# Revit family: BORGE_Вертикальная пожарная лестница_П-1
name_source: partatom
category: Обобщенные модели
units: mm (PartAtom-declared; Revit-internal decimal feet)

## family parameters
Всегда вертикально = Да
Заголовок OmniClass = Diffusers, Registers, and Grilles
Может служить основой для арматурных стержней = Нет
На основе рабочей плоскости = Нет
Номер OmniClass = 23.75.70.21.27.11
Общий = Нет
При загрузке вырезать с полостями = Нет
Размер круглого соединителя = Использовать диаметр
Тип детали = Нормальный
Точка расчета площади = Нет

## types (22) — shared parameters
ADSK_URL документации изделия = https://borge.pro
ADSK_URL страницы изделия = https://borge.pro
ADSK_Версия семейства = Rev1 2023-08
BIM Support_Разрабочик = BIM Support
BIM Support_Сайт = https://www.bim-support.ru
LT = BORGE_Снегозадержатель_Трубчатый
URL = https://borge.ru
Изготовитель = ООО «Борге», ООО «Бипро»
Описание = Максимальная высота лестницы 6м.

## per-type parameters (varying)
| type | ADSK_Материал | Code2 |
| Пожарная лестница_П1-1_Бело-алюминиевый_RAL 9006 | BOGRE_Уcловный_Коричневый шоколад_RAL 8017 | 10 |
| Пожарная лестница_П1-1_Чёрный матовый_RAL 9005 | BOGRE_Уcловный_Чёрный матовый_RAL 9005 | 2 |
| Пожарная лестница_П1-1_Чёрный_RAL 9005 | BOGRE_Уcловный_Чёрный_RAL 9005 | 3 |
| Пожарная лестница_П1-1_Сигнально-белый_RAL 9003 | BOGRE_Уcловный_Сигнально-белый_RAL 9003 | 4 |
| Пожарная лестница_П1-1_Окрашенный_NL 807 | BOGRE_Уcловный_Окрашенный_NL 807 | 5 |
| Пожарная лестница_П1-1_Окрашенный_NL 805 | BOGRE_Уcловный_Окрашенный_NL 805 | 6 |
| Пожарная лестница_П1-1_Серо-коричневый матовый_RAL 8019 | BOGRE_Уcловный_Серо-коричневый матовый_RAL 8019 | 7 |
| Пожарная лестница_П1-1_Серо-коричневый_RAL 8019 | BOGRE_Уcловный_Серо-коричневый_RAL 8019 | 8 |
| Пожарная лестница_П1-1_Коричневый шоколад матовый_RAL 8017 | BOGRE_Уcловный_Коричневый шоколад матовый_RAL 8017 | 9 |
| Пожарная лестница_П1-1_Коричневый шоколад_RAL 8017 | BOGRE_Уcловный_Коричневый шоколад_RAL 8017 | 10 |
| Пожарная лестница_П1-1_Терракотовый_RAL 8004 | BOGRE_Уcловный_Терракотовый_RAL 8004 | 11 |
| Пожарная лестница_П1-1_Серый графит матовый_RAL 7024 | BOGRE_Уcловный_Серый графит матовый_RAL 7024 | 12 |
| Пожарная лестница_П1-1_Серый графит_RAL 7024 | BOGRE_Уcловный_Серый графит_RAL 7024 | 13 |
| Пожарная лестница_П1-1_Антрацитово-серый_RAL 7016 | BOGRE_Уcловный_Антрацитово-серый_RAL 7016 | 14 |
| Пожарная лестница_П1-1_Сигнально-серый_RAL 7004 | BOGRE_Уcловный_Сигнально-серый_RAL 7004 | 15 |
| Пожарная лестница_П1-1_Зелёный мох_RAL 6005 | BOGRE_Уcловный_Зелёный мох_RAL 6005 | 16 |
| Пожарная лестница_П1-1_Лиственно-зеленый_RAL 6002 | BOGRE_Уcловный_Лиственно-зеленый_RAL 6002 | 17 |
| Пожарная лестница_П1-1_Сигнально-синий_RAL 5005 | BOGRE_Уcловный_Сигнально-синий_RAL 5005 | 18 |
| Пожарная лестница_П1-1_Серо-коричневый_RR 32 | BOGRE_Уcловный_Серо-коричневый_RR 32 | 19 |
| Пожарная лестница_П1-1_Коричнево-красный_RAL 3011 | BOGRE_Уcловный_Коричнево-красный_RAL 3011 | 20 |
| Пожарная лестница_П1-1_Красное вино_RAL 3005 | BOGRE_Уcловный_Красное вино_RAL 3005 | 21 |
| Пожарная лестница_П1-1_Рубиново-красный_RAL 3003 | BOGRE_Уcловный_Рубиново-красный_RAL 3003 | 22 |
